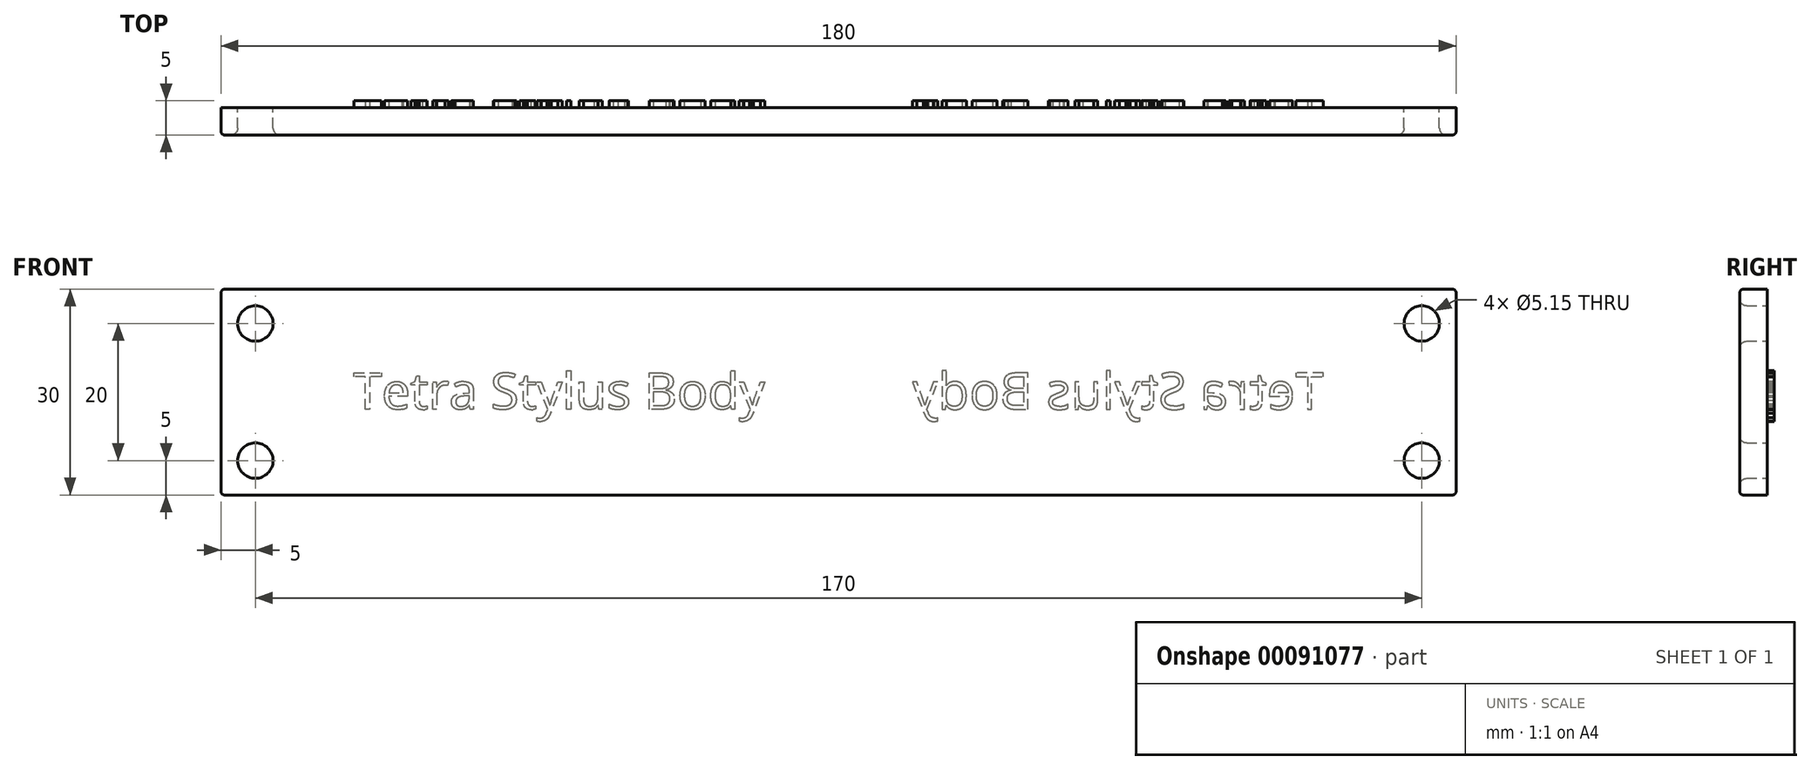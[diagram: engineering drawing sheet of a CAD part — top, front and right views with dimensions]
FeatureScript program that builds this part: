
annotation { "Feature Type Name" : "Feature", "Feature Type Description" : "" }
export const myFeature = defineFeature(function(context is Context, id is Id, definition is map)
    precondition{}
    {
        {
            var Q0;
            Q0=qCreatedBy(makeId("Front.planeOp"),FACE);
            var sketch = newSketch(context, id + "F0", { "sketchPlane" : qUnion([Q0])});
            skLineSegment(sketch, "E0.bottom", {"start": v(-90, -15) * mm, "end": v(90, -15) * mm});
            skLineSegment(sketch, "E0.top", {"start": v(-90, 15) * mm, "end": v(90, 15) * mm});
            skLineSegment(sketch, "E0.left", {"start": v(-90, -15) * mm, "end": v(-90, 15) * mm});
            skLineSegment(sketch, "E0.right", {"start": v(90, -15) * mm, "end": v(90, 15) * mm});
            skPoint(sketch, "E0.middle", {"position": v(0, 0) * mm});
            skCircle(sketch, "E1", {"center": v(-85, 10) * mm, "radius": 2.58 * mm});
            skPoint(sketch, "E2.start.orphan", {"position": v(-90, 0) * mm});
            skPoint(sketch, "E3.orphan", {"position": v(0, 15) * mm});
            skPoint(sketch, "E4.end.orphan", {"position": v(0, -15) * mm});
            skLineSegment(sketch, "E5", {"start": v(-90, 0) * mm, "end": v(0, 0) * mm, "construction": true});
            skLineSegment(sketch, "E6", {"start": v(0, 15) * mm, "end": v(0, -15) * mm, "construction": true});
            skCircle(sketch, "E7.MirrorC", {"center": v(-85, -10) * mm, "radius": 2.58 * mm});
            skCircle(sketch, "E8.MirrorC", {"center": v(85, 10) * mm, "radius": 2.58 * mm});
            skCircle(sketch, "E9.MirrorC", {"center": v(85, -10) * mm, "radius": 2.58 * mm});
            skSolve(sketch);
        }
        {
            var Q0;
            Q0=makeQuery(id+"F0.imprint","IMPRINT",FACE,{"disambiguationData":[TD([[makeQuery(id+"F0.imprint","IMPRINT",EDGE,{"derivedFrom":sQuery(id+"F0.wireOp",EDGE,"E0.bottom")}),1.0]])]});
            extrude(context, id + "F1", {"entities" : qUnion([Q0]), "depth" : 4 * mm});
        }
        {
            var Q0;
            Q0=makeQuery(id+"F1.opExtrude","CAP_EDGE",EDGE,{"disambiguationData":[OSD([sQuery(id+"F0.wireOp",EDGE,"E1")])],"isStart":false});
            var Q1;
            Q1=makeQuery(id+"F1.opExtrude","CAP_EDGE",EDGE,{"disambiguationData":[OSD([sQuery(id+"F0.wireOp",EDGE,"f5b72a5b-8583-449a-bdbf-9ac5a681e1fd0.MirrorC")])],"isStart":false});
            var Q2;
            Q2=makeQuery(id+"F1.opExtrude","CAP_EDGE",EDGE,{"disambiguationData":[OSD([sQuery(id+"F0.wireOp",EDGE,"2623e306-60f4-4522-aa65-1e3e8c2cf5b60.MirrorC")])],"isStart":false});
            var Q3;
            Q3=makeQuery(id+"F1.opExtrude","CAP_EDGE",EDGE,{"disambiguationData":[OSD([sQuery(id+"F0.wireOp",EDGE,"be81a34d-1d50-4ce7-a7a8-4484a1701fac0.MirrorC")])],"isStart":false});
            var Q4;
            Q4=makeQuery(id+"F1.opExtrude","CAP_EDGE",EDGE,{"disambiguationData":[OSD([sQuery(id+"F0.wireOp",EDGE,"E7.MirrorC")])],"isStart":false});
            var Q5;
            Q5=makeQuery(id+"F1.opExtrude","CAP_EDGE",EDGE,{"disambiguationData":[OSD([sQuery(id+"F0.wireOp",EDGE,"E8.MirrorC")])],"isStart":false});
            var Q6;
            Q6=makeQuery(id+"F1.opExtrude","CAP_EDGE",EDGE,{"disambiguationData":[OSD([sQuery(id+"F0.wireOp",EDGE,"E9.MirrorC")])],"isStart":false});
            fillet(context, id + "F2", {"entities" : qUnion([Q0, Q1, Q2, Q3, Q4, Q5, Q6]), "radius" : 1 * mm, "tangentPropagation" : true, "allowEdgeOverflow" : false});
        }
        {
            var Q0;
            Q0=makeQuery(id+"F1.opExtrude","CAP_EDGE",EDGE,{"disambiguationData":[OSD([sQuery(id+"F0.wireOp",EDGE,"E0.top")])],"isStart":false});
            var Q1;
            Q1=makeQuery(id+"F1.opExtrude","CAP_EDGE",EDGE,{"disambiguationData":[OSD([sQuery(id+"F0.wireOp",EDGE,"E0.left")])],"isStart":false});
            var Q2;
            Q2=makeQuery(id+"F1.opExtrude","CAP_EDGE",EDGE,{"disambiguationData":[OSD([sQuery(id+"F0.wireOp",EDGE,"E0.bottom")])],"isStart":false});
            var Q3;
            Q3=makeQuery(id+"F1.opExtrude","CAP_EDGE",EDGE,{"disambiguationData":[OSD([sQuery(id+"F0.wireOp",EDGE,"E0.right")])],"isStart":false});
            var Q4;
            Q4=makeQuery(id+"F1.opExtrude","SWEPT_EDGE",EDGE,{"disambiguationData":[OSD([sQuery(id+"F0.wireOp",EDGE,"E0.top"),sQuery(id+"F0.wireOp",EDGE,"E0.left")])]});
            var Q5;
            Q5=makeQuery(id+"F1.opExtrude","SWEPT_EDGE",EDGE,{"disambiguationData":[OSD([sQuery(id+"F0.wireOp",EDGE,"E0.bottom"),sQuery(id+"F0.wireOp",EDGE,"E0.left")])]});
            var Q6;
            Q6=makeQuery(id+"F1.opExtrude","SWEPT_EDGE",EDGE,{"disambiguationData":[OSD([sQuery(id+"F0.wireOp",EDGE,"E0.top"),sQuery(id+"F0.wireOp",EDGE,"E0.right")])]});
            var Q7;
            Q7=makeQuery(id+"F1.opExtrude","SWEPT_EDGE",EDGE,{"disambiguationData":[OSD([sQuery(id+"F0.wireOp",EDGE,"E0.bottom"),sQuery(id+"F0.wireOp",EDGE,"E0.right")])]});
            fillet(context, id + "F3", {"entities" : qUnion([Q0, Q1, Q2, Q3, Q4, Q5, Q6, Q7]), "radius" : .5 * mm, "tangentPropagation" : true, "allowEdgeOverflow" : false});
        }
        {
            var Q0;
            Q0=makeQuery(id+"F1.opExtrude","CAP_FACE",FACE,{"disambiguationData":[OSD([sQuery(id+"F0.wireOp",EDGE,"E0.bottom"),sQuery(id+"F0.wireOp",EDGE,"E0.top"),sQuery(id+"F0.wireOp",EDGE,"E0.left"),sQuery(id+"F0.wireOp",EDGE,"E0.right"),sQuery(id+"F0.wireOp",EDGE,"E1"),sQuery(id+"F0.wireOp",EDGE,"E7.MirrorC"),sQuery(id+"F0.wireOp",EDGE,"E8.MirrorC"),sQuery(id+"F0.wireOp",EDGE,"E9.MirrorC")])],"isStart":true});
            var sketch = newSketch(context, id + "F4", { "sketchPlane" : qUnion([Q0])});
            skText(sketch, "E10", { "text": "Tetra Stylus Body", "fontName": "OpenSans-Regular.ttf"});
            skLineSegment(sketch, "E11", {"start": v(0, 15) * mm, "end": v(0, -15) * mm, "construction": true});
            const initialGuessF4  = {"E10": [-0.0707, -0.0025, 1, 0, 0.00535]};
            skSetInitialGuess(sketch, initialGuessF4);
            skSolve(sketch);
        }
        {
            var Q0;
            Q0=qSketchRegion(id+"F4",true);
            extrude(context, id + "F5", {"entities" : qUnion([Q0]), "operationType" : NewBodyOperationType.ADD, "depth" : 1 * mm});
        }
        {
            var Q0;
            Q0=makeQuery(id+"F1.opExtrude","SWEPT_BODY",BODY,{"disambiguationData":[OSD([sQuery(id+"F0.wireOp",EDGE,"E0.bottom"),sQuery(id+"F0.wireOp",EDGE,"E0.top"),sQuery(id+"F0.wireOp",EDGE,"E0.left"),sQuery(id+"F0.wireOp",EDGE,"E0.right"),sQuery(id+"F0.wireOp",EDGE,"E1"),sQuery(id+"F0.wireOp",EDGE,"E7.MirrorC"),sQuery(id+"F0.wireOp",EDGE,"E8.MirrorC"),sQuery(id+"F0.wireOp",EDGE,"E9.MirrorC")])]});
            var Q1;
            Q1=makeQuery(id+"F5.opExtrude","SWEPT_FACE",FACE,{"disambiguationData":[OSD([sQuery(id+"F4.wireOp",EDGE,"E10.sketch_text.stroke-94")])]});
            var Q2;
            Q2=makeQuery(id+"F5.opExtrude","SWEPT_FACE",FACE,{"disambiguationData":[OSD([sQuery(id+"F4.wireOp",EDGE,"E10.sketch_text.stroke-169")])]});
            var Q3;
            Q3=makeQuery(id+"F5.opExtrude","SWEPT_FACE",FACE,{"disambiguationData":[OSD([sQuery(id+"F4.wireOp",EDGE,"E10.sketch_text.stroke-185")])]});
            var Q4;
            Q4=makeQuery(id+"F5.opExtrude","SWEPT_FACE",FACE,{"disambiguationData":[OSD([sQuery(id+"F4.wireOp",EDGE,"E10.sketch_text.stroke-125")])]});
            var Q5;
            Q5=makeQuery(id+"F5.opExtrude","SWEPT_FACE",FACE,{"disambiguationData":[OSD([sQuery(id+"F4.wireOp",EDGE,"E10.sketch_text.stroke-155")])]});
            var Q6;
            Q6=makeQuery(id+"F5.opExtrude","SWEPT_FACE",FACE,{"disambiguationData":[OSD([sQuery(id+"F4.wireOp",EDGE,"E10.sketch_text.stroke-65")])]});
            var Q7;
            Q7=makeQuery(id+"F5.opExtrude","SWEPT_FACE",FACE,{"disambiguationData":[OSD([sQuery(id+"F4.wireOp",EDGE,"E10.sketch_text.stroke-81")])]});
            var Q8;
            Q8=makeQuery(id+"F5.opExtrude","SWEPT_FACE",FACE,{"disambiguationData":[OSD([sQuery(id+"F4.wireOp",EDGE,"E10.sketch_text.stroke-67")])]});
            var Q9;
            Q9=makeQuery(id+"F5.opExtrude","SWEPT_FACE",FACE,{"disambiguationData":[OSD([sQuery(id+"F4.wireOp",EDGE,"E10.sketch_text.stroke-99")])]});
            var Q10;
            Q10=makeQuery(id+"F5.opExtrude","SWEPT_FACE",FACE,{"disambiguationData":[OSD([sQuery(id+"F4.wireOp",EDGE,"E10.sketch_text.stroke-127")])]});
            var Q11;
            Q11=makeQuery(id+"F5.opExtrude","SWEPT_FACE",FACE,{"disambiguationData":[OSD([sQuery(id+"F4.wireOp",EDGE,"E10.sketch_text.stroke-10")])]});
            var Q12;
            Q12=makeQuery(id+"F5.opExtrude","CAP_FACE",FACE,{"disambiguationData":[OSD([sQuery(id+"F4.wireOp",EDGE,"E10.sketch_text.stroke-9"),sQuery(id+"F4.wireOp",EDGE,"E10.sketch_text.stroke-10"),sQuery(id+"F4.wireOp",EDGE,"E10.sketch_text.stroke-11"),sQuery(id+"F4.wireOp",EDGE,"E10.sketch_text.stroke-12")])],"isStart":false});
            var Q13;
            Q13=makeQuery(id+"F5.opExtrude","SWEPT_FACE",FACE,{"disambiguationData":[OSD([sQuery(id+"F4.wireOp",EDGE,"E10.sketch_text.stroke-154")])]});
            var Q14;
            Q14=makeQuery(id+"F5.opExtrude","SWEPT_FACE",FACE,{"disambiguationData":[OSD([sQuery(id+"F4.wireOp",EDGE,"E10.sketch_text.stroke-1")])]});
            var Q15;
            Q15=makeQuery(id+"F5.opExtrude","CAP_FACE",FACE,{"disambiguationData":[OSD([sQuery(id+"F4.wireOp",EDGE,"E10.sketch_text.stroke-124"),sQuery(id+"F4.wireOp",EDGE,"E10.sketch_text.stroke-125"),sQuery(id+"F4.wireOp",EDGE,"E10.sketch_text.stroke-126"),sQuery(id+"F4.wireOp",EDGE,"E10.sketch_text.stroke-127"),sQuery(id+"F4.wireOp",EDGE,"E10.sketch_text.stroke-128"),sQuery(id+"F4.wireOp",EDGE,"E10.sketch_text.stroke-129"),sQuery(id+"F4.wireOp",EDGE,"E10.sketch_text.stroke-130"),sQuery(id+"F4.wireOp",EDGE,"E10.sketch_text.stroke-131"),sQuery(id+"F4.wireOp",EDGE,"E10.sketch_text.stroke-132"),sQuery(id+"F4.wireOp",EDGE,"E10.sketch_text.stroke-133"),sQuery(id+"F4.wireOp",EDGE,"E10.sketch_text.stroke-134"),sQuery(id+"F4.wireOp",EDGE,"E10.sketch_text.stroke-135"),sQuery(id+"F4.wireOp",EDGE,"E10.sketch_text.stroke-136"),sQuery(id+"F4.wireOp",EDGE,"E10.sketch_text.stroke-137"),sQuery(id+"F4.wireOp",EDGE,"E10.sketch_text.stroke-138")])],"isStart":false});
            var Q16;
            Q16=makeQuery(id+"F5.opExtrude","CAP_FACE",FACE,{"disambiguationData":[OSD([sQuery(id+"F4.wireOp",EDGE,"E10.sketch_text.stroke-34"),sQuery(id+"F4.wireOp",EDGE,"E10.sketch_text.stroke-35"),sQuery(id+"F4.wireOp",EDGE,"E10.sketch_text.stroke-36"),sQuery(id+"F4.wireOp",EDGE,"E10.sketch_text.stroke-37"),sQuery(id+"F4.wireOp",EDGE,"E10.sketch_text.stroke-38"),sQuery(id+"F4.wireOp",EDGE,"E10.sketch_text.stroke-39"),sQuery(id+"F4.wireOp",EDGE,"E10.sketch_text.stroke-40"),sQuery(id+"F4.wireOp",EDGE,"E10.sketch_text.stroke-41"),sQuery(id+"F4.wireOp",EDGE,"E10.sketch_text.stroke-42"),sQuery(id+"F4.wireOp",EDGE,"E10.sketch_text.stroke-43"),sQuery(id+"F4.wireOp",EDGE,"E10.sketch_text.stroke-44"),sQuery(id+"F4.wireOp",EDGE,"E10.sketch_text.stroke-45"),sQuery(id+"F4.wireOp",EDGE,"E10.sketch_text.stroke-46"),sQuery(id+"F4.wireOp",EDGE,"E10.sketch_text.stroke-47"),sQuery(id+"F4.wireOp",EDGE,"E10.sketch_text.stroke-48"),sQuery(id+"F4.wireOp",EDGE,"E10.sketch_text.stroke-49"),sQuery(id+"F4.wireOp",EDGE,"E10.sketch_text.stroke-50"),sQuery(id+"F4.wireOp",EDGE,"E10.sketch_text.stroke-51"),sQuery(id+"F4.wireOp",EDGE,"E10.sketch_text.stroke-52"),sQuery(id+"F4.wireOp",EDGE,"E10.sketch_text.stroke-53"),sQuery(id+"F4.wireOp",EDGE,"E10.sketch_text.stroke-54"),sQuery(id+"F4.wireOp",EDGE,"E10.sketch_text.stroke-55"),sQuery(id+"F4.wireOp",EDGE,"E10.sketch_text.stroke-56"),sQuery(id+"F4.wireOp",EDGE,"E10.sketch_text.stroke-57"),sQuery(id+"F4.wireOp",EDGE,"E10.sketch_text.stroke-58"),sQuery(id+"F4.wireOp",EDGE,"E10.sketch_text.stroke-59"),sQuery(id+"F4.wireOp",EDGE,"E10.sketch_text.stroke-60")])],"isStart":false});
            var Q17;
            Q17=makeQuery(id+"F5.opExtrude","SWEPT_FACE",FACE,{"disambiguationData":[OSD([sQuery(id+"F4.wireOp",EDGE,"E10.sketch_text.stroke-50")])]});
            var Q18;
            Q18=makeQuery(id+"F5.opExtrude","SWEPT_FACE",FACE,{"disambiguationData":[OSD([sQuery(id+"F4.wireOp",EDGE,"E10.sketch_text.stroke-2")])]});
            var Q19;
            Q19=makeQuery(id+"F5.opExtrude","SWEPT_FACE",FACE,{"disambiguationData":[OSD([sQuery(id+"F4.wireOp",EDGE,"E10.sketch_text.stroke-3")])]});
            var Q20;
            Q20=makeQuery(id+"F5.opExtrude","SWEPT_FACE",FACE,{"disambiguationData":[OSD([sQuery(id+"F4.wireOp",EDGE,"E10.sketch_text.stroke-5")])]});
            var Q21;
            Q21=makeQuery(id+"F5.opExtrude","SWEPT_FACE",FACE,{"disambiguationData":[OSD([sQuery(id+"F4.wireOp",EDGE,"E10.sketch_text.stroke-8")])]});
            var Q22;
            Q22=makeQuery(id+"F5.opExtrude","SWEPT_FACE",FACE,{"disambiguationData":[OSD([sQuery(id+"F4.wireOp",EDGE,"E10.sketch_text.stroke-98")])]});
            var Q23;
            Q23=makeQuery(id+"F5.opExtrude","SWEPT_FACE",FACE,{"disambiguationData":[OSD([sQuery(id+"F4.wireOp",EDGE,"E10.sketch_text.stroke-66")])]});
            var Q24;
            Q24=makeQuery(id+"F5.opExtrude","SWEPT_FACE",FACE,{"disambiguationData":[OSD([sQuery(id+"F4.wireOp",EDGE,"E10.sketch_text.stroke-153")])]});
            var Q25;
            Q25=makeQuery(id+"F5.opExtrude","SWEPT_FACE",FACE,{"disambiguationData":[OSD([sQuery(id+"F4.wireOp",EDGE,"E10.sketch_text.stroke-126")])]});
            var Q26;
            Q26=makeQuery(id+"F5.opExtrude","SWEPT_FACE",FACE,{"disambiguationData":[OSD([sQuery(id+"F4.wireOp",EDGE,"E10.sketch_text.stroke-183")])]});
            var Q27;
            Q27=makeQuery(id+"F5.opExtrude","SWEPT_FACE",FACE,{"disambiguationData":[OSD([sQuery(id+"F4.wireOp",EDGE,"E10.sketch_text.stroke-109")])]});
            var Q28;
            Q28=makeQuery(id+"F5.opExtrude","SWEPT_FACE",FACE,{"disambiguationData":[OSD([sQuery(id+"F4.wireOp",EDGE,"E10.sketch_text.stroke-186")])]});
            var Q29;
            Q29=makeQuery(id+"F5.opExtrude","SWEPT_FACE",FACE,{"disambiguationData":[OSD([sQuery(id+"F4.wireOp",EDGE,"E10.sketch_text.stroke-79")])]});
            var Q30;
            Q30=makeQuery(id+"F5.opExtrude","SWEPT_FACE",FACE,{"disambiguationData":[OSD([sQuery(id+"F4.wireOp",EDGE,"E10.sketch_text.stroke-110")])]});
            var Q31;
            Q31=makeQuery(id+"F5.opExtrude","SWEPT_FACE",FACE,{"disambiguationData":[OSD([sQuery(id+"F4.wireOp",EDGE,"E10.sketch_text.stroke-38")])]});
            var Q32;
            Q32=makeQuery(id+"F5.opExtrude","SWEPT_FACE",FACE,{"disambiguationData":[OSD([sQuery(id+"F4.wireOp",EDGE,"E10.sketch_text.stroke-24")])]});
            var Q33;
            Q33=makeQuery(id+"F5.opExtrude","SWEPT_FACE",FACE,{"disambiguationData":[OSD([sQuery(id+"F4.wireOp",EDGE,"E10.sketch_text.stroke-12")])]});
            var Q34;
            Q34=makeQuery(id+"F5.opExtrude","SWEPT_FACE",FACE,{"disambiguationData":[OSD([sQuery(id+"F4.wireOp",EDGE,"E10.sketch_text.stroke-100")])]});
            var Q35;
            Q35=makeQuery(id+"F5.opExtrude","SWEPT_FACE",FACE,{"disambiguationData":[OSD([sQuery(id+"F4.wireOp",EDGE,"E10.sketch_text.stroke-158")])]});
            var Q36;
            Q36=makeQuery(id+"F5.opExtrude","SWEPT_FACE",FACE,{"disambiguationData":[OSD([sQuery(id+"F4.wireOp",EDGE,"E10.sketch_text.stroke-142")])]});
            var Q37;
            Q37=makeQuery(id+"F5.opExtrude","SWEPT_FACE",FACE,{"disambiguationData":[OSD([sQuery(id+"F4.wireOp",EDGE,"E10.sketch_text.stroke-54")])]});
            var Q38;
            Q38=makeQuery(id+"F5.opExtrude","SWEPT_FACE",FACE,{"disambiguationData":[OSD([sQuery(id+"F4.wireOp",EDGE,"E10.sketch_text.stroke-25")])]});
            var Q39;
            Q39=makeQuery(id+"F5.opExtrude","SWEPT_FACE",FACE,{"disambiguationData":[OSD([sQuery(id+"F4.wireOp",EDGE,"E10.sketch_text.stroke-101")])]});
            var Q40;
            Q40=makeQuery(id+"F5.opExtrude","SWEPT_FACE",FACE,{"disambiguationData":[OSD([sQuery(id+"F4.wireOp",EDGE,"E10.sketch_text.stroke-69")])]});
            var Q41;
            Q41=makeQuery(id+"F5.opExtrude","SWEPT_FACE",FACE,{"disambiguationData":[OSD([sQuery(id+"F4.wireOp",EDGE,"E10.sketch_text.stroke-159")])]});
            var Q42;
            Q42=makeQuery(id+"F5.opExtrude","SWEPT_FACE",FACE,{"disambiguationData":[OSD([sQuery(id+"F4.wireOp",EDGE,"E10.sketch_text.stroke-85")])]});
            var Q43;
            Q43=makeQuery(id+"F5.opExtrude","SWEPT_FACE",FACE,{"disambiguationData":[OSD([sQuery(id+"F4.wireOp",EDGE,"E10.sketch_text.stroke-173")])]});
            var Q44;
            Q44=makeQuery(id+"F5.opExtrude","SWEPT_FACE",FACE,{"disambiguationData":[OSD([sQuery(id+"F4.wireOp",EDGE,"E10.sketch_text.stroke-40")])]});
            var Q45;
            Q45=makeQuery(id+"F5.opExtrude","SWEPT_FACE",FACE,{"disambiguationData":[OSD([sQuery(id+"F4.wireOp",EDGE,"E10.sketch_text.stroke-102")])]});
            var Q46;
            Q46=makeQuery(id+"F5.opExtrude","SWEPT_FACE",FACE,{"disambiguationData":[OSD([sQuery(id+"F4.wireOp",EDGE,"E10.sketch_text.stroke-86")])]});
            var Q47;
            Q47=makeQuery(id+"F5.opExtrude","SWEPT_FACE",FACE,{"disambiguationData":[OSD([sQuery(id+"F4.wireOp",EDGE,"E10.sketch_text.stroke-130")])]});
            var Q48;
            Q48=makeQuery(id+"F5.opExtrude","SWEPT_FACE",FACE,{"disambiguationData":[OSD([sQuery(id+"F4.wireOp",EDGE,"E10.sketch_text.stroke-103")])]});
            var Q49;
            Q49=makeQuery(id+"F5.opExtrude","SWEPT_FACE",FACE,{"disambiguationData":[OSD([sQuery(id+"F4.wireOp",EDGE,"E10.sketch_text.stroke-87")])]});
            var Q50;
            Q50=makeQuery(id+"F5.opExtrude","SWEPT_FACE",FACE,{"disambiguationData":[OSD([sQuery(id+"F4.wireOp",EDGE,"E10.sketch_text.stroke-145")])]});
            var Q51;
            Q51=makeQuery(id+"F5.opExtrude","SWEPT_FACE",FACE,{"disambiguationData":[OSD([sQuery(id+"F4.wireOp",EDGE,"E10.sketch_text.stroke-131")])]});
            var Q52;
            Q52=makeQuery(id+"F5.opExtrude","SWEPT_FACE",FACE,{"disambiguationData":[OSD([sQuery(id+"F4.wireOp",EDGE,"E10.sketch_text.stroke-28")])]});
            var Q53;
            Q53=makeQuery(id+"F5.opExtrude","SWEPT_FACE",FACE,{"disambiguationData":[OSD([sQuery(id+"F4.wireOp",EDGE,"E10.sketch_text.stroke-14")])]});
            var Q54;
            Q54=makeQuery(id+"F5.opExtrude","SWEPT_FACE",FACE,{"disambiguationData":[OSD([sQuery(id+"F4.wireOp",EDGE,"E10.sketch_text.stroke-88")])]});
            var Q55;
            Q55=makeQuery(id+"F5.opExtrude","SWEPT_FACE",FACE,{"disambiguationData":[OSD([sQuery(id+"F4.wireOp",EDGE,"E10.sketch_text.stroke-162")])]});
            var Q56;
            Q56=makeQuery(id+"F5.opExtrude","SWEPT_FACE",FACE,{"disambiguationData":[OSD([sQuery(id+"F4.wireOp",EDGE,"E10.sketch_text.stroke-176")])]});
            var Q57;
            Q57=makeQuery(id+"F5.opExtrude","SWEPT_FACE",FACE,{"disambiguationData":[OSD([sQuery(id+"F4.wireOp",EDGE,"E10.sketch_text.stroke-73")])]});
            var Q58;
            Q58=makeQuery(id+"F5.opExtrude","SWEPT_FACE",FACE,{"disambiguationData":[OSD([sQuery(id+"F4.wireOp",EDGE,"E10.sketch_text.stroke-59")])]});
            var Q59;
            Q59=makeQuery(id+"F5.opExtrude","SWEPT_FACE",FACE,{"disambiguationData":[OSD([sQuery(id+"F4.wireOp",EDGE,"E10.sketch_text.stroke-133")])]});
            var Q60;
            Q60=makeQuery(id+"F5.opExtrude","SWEPT_FACE",FACE,{"disambiguationData":[OSD([sQuery(id+"F4.wireOp",EDGE,"E10.sketch_text.stroke-119")])]});
            var Q61;
            Q61=makeQuery(id+"F5.opExtrude","SWEPT_FACE",FACE,{"disambiguationData":[OSD([sQuery(id+"F4.wireOp",EDGE,"E10.sketch_text.stroke-74")])]});
            var Q62;
            Q62=makeQuery(id+"F5.opExtrude","SWEPT_FACE",FACE,{"disambiguationData":[OSD([sQuery(id+"F4.wireOp",EDGE,"E10.sketch_text.stroke-44")])]});
            var Q63;
            Q63=makeQuery(id+"F5.opExtrude","SWEPT_FACE",FACE,{"disambiguationData":[OSD([sQuery(id+"F4.wireOp",EDGE,"E10.sketch_text.stroke-120")])]});
            var Q64;
            Q64=makeQuery(id+"F5.opExtrude","SWEPT_FACE",FACE,{"disambiguationData":[OSD([sQuery(id+"F4.wireOp",EDGE,"E10.sketch_text.stroke-90")])]});
            var Q65;
            Q65=makeQuery(id+"F5.opExtrude","SWEPT_FACE",FACE,{"disambiguationData":[OSD([sQuery(id+"F4.wireOp",EDGE,"E10.sketch_text.stroke-178")])]});
            var Q66;
            Q66=makeQuery(id+"F5.opExtrude","SWEPT_FACE",FACE,{"disambiguationData":[OSD([sQuery(id+"F4.wireOp",EDGE,"E10.sketch_text.stroke-45")])]});
            var Q67;
            Q67=makeQuery(id+"F5.opExtrude","SWEPT_FACE",FACE,{"disambiguationData":[OSD([sQuery(id+"F4.wireOp",EDGE,"E10.sketch_text.stroke-31")])]});
            var Q68;
            Q68=makeQuery(id+"F5.opExtrude","SWEPT_FACE",FACE,{"disambiguationData":[OSD([sQuery(id+"F4.wireOp",EDGE,"E10.sketch_text.stroke-135")])]});
            var Q69;
            Q69=makeQuery(id+"F5.opExtrude","SWEPT_FACE",FACE,{"disambiguationData":[OSD([sQuery(id+"F4.wireOp",EDGE,"E10.sketch_text.stroke-179")])]});
            var Q70;
            Q70=makeQuery(id+"F5.opExtrude","SWEPT_FACE",FACE,{"disambiguationData":[OSD([sQuery(id+"F4.wireOp",EDGE,"E10.sketch_text.stroke-165")])]});
            var Q71;
            Q71=makeQuery(id+"F5.opExtrude","SWEPT_FACE",FACE,{"disambiguationData":[OSD([sQuery(id+"F4.wireOp",EDGE,"E10.sketch_text.stroke-149")])]});
            var Q72;
            Q72=makeQuery(id+"F5.opExtrude","SWEPT_FACE",FACE,{"disambiguationData":[OSD([sQuery(id+"F4.wireOp",EDGE,"E10.sketch_text.stroke-136")])]});
            var Q73;
            Q73=makeQuery(id+"F5.opExtrude","SWEPT_FACE",FACE,{"disambiguationData":[OSD([sQuery(id+"F4.wireOp",EDGE,"E10.sketch_text.stroke-122")])]});
            var Q74;
            Q74=makeQuery(id+"F5.opExtrude","SWEPT_FACE",FACE,{"disambiguationData":[OSD([sQuery(id+"F4.wireOp",EDGE,"E10.sketch_text.stroke-106")])]});
            var Q75;
            Q75=makeQuery(id+"F5.opExtrude","SWEPT_FACE",FACE,{"disambiguationData":[OSD([sQuery(id+"F4.wireOp",EDGE,"E10.sketch_text.stroke-180")])]});
            var Q76;
            Q76=makeQuery(id+"F5.opExtrude","SWEPT_FACE",FACE,{"disambiguationData":[OSD([sQuery(id+"F4.wireOp",EDGE,"E10.sketch_text.stroke-166")])]});
            var Q77;
            Q77=makeQuery(id+"F5.opExtrude","SWEPT_FACE",FACE,{"disambiguationData":[OSD([sQuery(id+"F4.wireOp",EDGE,"E10.sketch_text.stroke-150")])]});
            var Q78;
            Q78=makeQuery(id+"F5.opExtrude","SWEPT_FACE",FACE,{"disambiguationData":[OSD([sQuery(id+"F4.wireOp",EDGE,"E10.sketch_text.stroke-76")])]});
            var Q79;
            Q79=makeQuery(id+"F5.opExtrude","SWEPT_FACE",FACE,{"disambiguationData":[OSD([sQuery(id+"F4.wireOp",EDGE,"E10.sketch_text.stroke-32")])]});
            var Q80;
            Q80=makeQuery(id+"F5.opExtrude","SWEPT_FACE",FACE,{"disambiguationData":[OSD([sQuery(id+"F4.wireOp",EDGE,"E10.sketch_text.stroke-181")])]});
            var Q81;
            Q81=makeQuery(id+"F5.opExtrude","SWEPT_FACE",FACE,{"disambiguationData":[OSD([sQuery(id+"F4.wireOp",EDGE,"E10.sketch_text.stroke-47")])]});
            var Q82;
            Q82=makeQuery(id+"F5.opExtrude","SWEPT_FACE",FACE,{"disambiguationData":[OSD([sQuery(id+"F4.wireOp",EDGE,"E10.sketch_text.stroke-123")])]});
            var Q83;
            Q83=makeQuery(id+"F5.opExtrude","SWEPT_FACE",FACE,{"disambiguationData":[OSD([sQuery(id+"F4.wireOp",EDGE,"E10.sketch_text.stroke-107")])]});
            var Q84;
            Q84=makeQuery(id+"F5.opExtrude","SWEPT_FACE",FACE,{"disambiguationData":[OSD([sQuery(id+"F4.wireOp",EDGE,"E10.sketch_text.stroke-48")])]});
            var Q85;
            Q85=makeQuery(id+"F5.opExtrude","SWEPT_FACE",FACE,{"disambiguationData":[OSD([sQuery(id+"F4.wireOp",EDGE,"E10.sketch_text.stroke-124")])]});
            var Q86;
            Q86=makeQuery(id+"F5.opExtrude","SWEPT_FACE",FACE,{"disambiguationData":[OSD([sQuery(id+"F4.wireOp",EDGE,"E10.sketch_text.stroke-108")])]});
            var Q87;
            Q87=makeQuery(id+"F5.opExtrude","CAP_FACE",FACE,{"disambiguationData":[OSD([sQuery(id+"F4.wireOp",EDGE,"E10.sketch_text.stroke-139"),sQuery(id+"F4.wireOp",EDGE,"E10.sketch_text.stroke-140"),sQuery(id+"F4.wireOp",EDGE,"E10.sketch_text.stroke-141"),sQuery(id+"F4.wireOp",EDGE,"E10.sketch_text.stroke-142"),sQuery(id+"F4.wireOp",EDGE,"E10.sketch_text.stroke-143"),sQuery(id+"F4.wireOp",EDGE,"E10.sketch_text.stroke-144"),sQuery(id+"F4.wireOp",EDGE,"E10.sketch_text.stroke-145"),sQuery(id+"F4.wireOp",EDGE,"E10.sketch_text.stroke-146"),sQuery(id+"F4.wireOp",EDGE,"E10.sketch_text.stroke-147"),sQuery(id+"F4.wireOp",EDGE,"E10.sketch_text.stroke-148"),sQuery(id+"F4.wireOp",EDGE,"E10.sketch_text.stroke-149"),sQuery(id+"F4.wireOp",EDGE,"E10.sketch_text.stroke-150"),sQuery(id+"F4.wireOp",EDGE,"E10.sketch_text.stroke-151"),sQuery(id+"F4.wireOp",EDGE,"E10.sketch_text.stroke-152"),sQuery(id+"F4.wireOp",EDGE,"E10.sketch_text.stroke-153"),sQuery(id+"F4.wireOp",EDGE,"E10.sketch_text.stroke-154"),sQuery(id+"F4.wireOp",EDGE,"E10.sketch_text.stroke-155"),sQuery(id+"F4.wireOp",EDGE,"E10.sketch_text.stroke-156"),sQuery(id+"F4.wireOp",EDGE,"E10.sketch_text.stroke-157"),sQuery(id+"F4.wireOp",EDGE,"E10.sketch_text.stroke-158"),sQuery(id+"F4.wireOp",EDGE,"E10.sketch_text.stroke-159"),sQuery(id+"F4.wireOp",EDGE,"E10.sketch_text.stroke-160"),sQuery(id+"F4.wireOp",EDGE,"E10.sketch_text.stroke-161"),sQuery(id+"F4.wireOp",EDGE,"E10.sketch_text.stroke-162"),sQuery(id+"F4.wireOp",EDGE,"E10.sketch_text.stroke-163"),sQuery(id+"F4.wireOp",EDGE,"E10.sketch_text.stroke-164"),sQuery(id+"F4.wireOp",EDGE,"E10.sketch_text.stroke-165")])],"isStart":false});
            var Q88;
            Q88=makeQuery(id+"F5.opExtrude","CAP_FACE",FACE,{"disambiguationData":[OSD([sQuery(id+"F4.wireOp",EDGE,"E10.sketch_text.stroke-21"),sQuery(id+"F4.wireOp",EDGE,"E10.sketch_text.stroke-22"),sQuery(id+"F4.wireOp",EDGE,"E10.sketch_text.stroke-23"),sQuery(id+"F4.wireOp",EDGE,"E10.sketch_text.stroke-24"),sQuery(id+"F4.wireOp",EDGE,"E10.sketch_text.stroke-25"),sQuery(id+"F4.wireOp",EDGE,"E10.sketch_text.stroke-26"),sQuery(id+"F4.wireOp",EDGE,"E10.sketch_text.stroke-27"),sQuery(id+"F4.wireOp",EDGE,"E10.sketch_text.stroke-28"),sQuery(id+"F4.wireOp",EDGE,"E10.sketch_text.stroke-29"),sQuery(id+"F4.wireOp",EDGE,"E10.sketch_text.stroke-30"),sQuery(id+"F4.wireOp",EDGE,"E10.sketch_text.stroke-31"),sQuery(id+"F4.wireOp",EDGE,"E10.sketch_text.stroke-32"),sQuery(id+"F4.wireOp",EDGE,"E10.sketch_text.stroke-33")])],"isStart":false});
            var Q89;
            Q89=makeQuery(id+"F5.opExtrude","SWEPT_FACE",FACE,{"disambiguationData":[OSD([sQuery(id+"F4.wireOp",EDGE,"E10.sketch_text.stroke-113")])]});
            var Q90;
            Q90=makeQuery(id+"F5.opExtrude","SWEPT_FACE",FACE,{"disambiguationData":[OSD([sQuery(id+"F4.wireOp",EDGE,"E10.sketch_text.stroke-37")])]});
            var Q91;
            Q91=makeQuery(id+"F5.opExtrude","SWEPT_FACE",FACE,{"disambiguationData":[OSD([sQuery(id+"F4.wireOp",EDGE,"E10.sketch_text.stroke-187")])]});
            var Q92;
            Q92=makeQuery(id+"F5.opExtrude","SWEPT_FACE",FACE,{"disambiguationData":[OSD([sQuery(id+"F4.wireOp",EDGE,"E10.sketch_text.stroke-0")])]});
            var Q93;
            Q93=makeQuery(id+"F5.opExtrude","SWEPT_FACE",FACE,{"disambiguationData":[OSD([sQuery(id+"F4.wireOp",EDGE,"E10.sketch_text.stroke-4")])]});
            var Q94;
            Q94=makeQuery(id+"F5.opExtrude","SWEPT_FACE",FACE,{"disambiguationData":[OSD([sQuery(id+"F4.wireOp",EDGE,"E10.sketch_text.stroke-82")])]});
            var Q95;
            Q95=makeQuery(id+"F5.opExtrude","SWEPT_FACE",FACE,{"disambiguationData":[OSD([sQuery(id+"F4.wireOp",EDGE,"E10.sketch_text.stroke-52")])]});
            var Q96;
            Q96=makeQuery(id+"F5.opExtrude","SWEPT_FACE",FACE,{"disambiguationData":[OSD([sQuery(id+"F4.wireOp",EDGE,"E10.sketch_text.stroke-49")])]});
            var Q97;
            Q97=makeQuery(id+"F5.opExtrude","SWEPT_FACE",FACE,{"disambiguationData":[OSD([sQuery(id+"F4.wireOp",EDGE,"E10.sketch_text.stroke-63")])]});
            var Q98;
            Q98=makeQuery(id+"F5.opExtrude","SWEPT_FACE",FACE,{"disambiguationData":[OSD([sQuery(id+"F4.wireOp",EDGE,"E10.sketch_text.stroke-21")])]});
            var Q99;
            Q99=makeQuery(id+"F5.opExtrude","SWEPT_FACE",FACE,{"disambiguationData":[OSD([sQuery(id+"F4.wireOp",EDGE,"E10.sketch_text.stroke-128")])]});
            var Q100;
            Q100=makeQuery(id+"F5.opExtrude","SWEPT_FACE",FACE,{"disambiguationData":[OSD([sQuery(id+"F4.wireOp",EDGE,"E10.sketch_text.stroke-55")])]});
            var Q101;
            Q101=makeQuery(id+"F5.opExtrude","SWEPT_FACE",FACE,{"disambiguationData":[OSD([sQuery(id+"F4.wireOp",EDGE,"E10.sketch_text.stroke-26")])]});
            var Q102;
            Q102=makeQuery(id+"F5.opExtrude","SWEPT_FACE",FACE,{"disambiguationData":[OSD([sQuery(id+"F4.wireOp",EDGE,"E10.sketch_text.stroke-174")])]});
            var Q103;
            Q103=makeQuery(id+"F5.opExtrude","SWEPT_FACE",FACE,{"disambiguationData":[OSD([sQuery(id+"F4.wireOp",EDGE,"E10.sketch_text.stroke-104")])]});
            var Q104;
            Q104=makeQuery(id+"F5.opExtrude","SWEPT_FACE",FACE,{"disambiguationData":[OSD([sQuery(id+"F4.wireOp",EDGE,"E10.sketch_text.stroke-72")])]});
            var Q105;
            Q105=makeQuery(id+"F5.opExtrude","SWEPT_FACE",FACE,{"disambiguationData":[OSD([sQuery(id+"F4.wireOp",EDGE,"E10.sketch_text.stroke-132")])]});
            var Q106;
            Q106=makeQuery(id+"F5.opExtrude","SWEPT_FACE",FACE,{"disambiguationData":[OSD([sQuery(id+"F4.wireOp",EDGE,"E10.sketch_text.stroke-43")])]});
            var Q107;
            Q107=makeQuery(id+"F5.opExtrude","SWEPT_FACE",FACE,{"disambiguationData":[OSD([sQuery(id+"F4.wireOp",EDGE,"E10.sketch_text.stroke-15")])]});
            var Q108;
            Q108=makeQuery(id+"F5.opExtrude","SWEPT_FACE",FACE,{"disambiguationData":[OSD([sQuery(id+"F4.wireOp",EDGE,"E10.sketch_text.stroke-89")])]});
            var Q109;
            Q109=makeQuery(id+"F5.opExtrude","SWEPT_FACE",FACE,{"disambiguationData":[OSD([sQuery(id+"F4.wireOp",EDGE,"E10.sketch_text.stroke-163")])]});
            var Q110;
            Q110=makeQuery(id+"F5.opExtrude","SWEPT_FACE",FACE,{"disambiguationData":[OSD([sQuery(id+"F4.wireOp",EDGE,"E10.sketch_text.stroke-30")])]});
            var Q111;
            Q111=makeQuery(id+"F5.opExtrude","SWEPT_FACE",FACE,{"disambiguationData":[OSD([sQuery(id+"F4.wireOp",EDGE,"E10.sketch_text.stroke-134")])]});
            var Q112;
            Q112=makeQuery(id+"F5.opExtrude","SWEPT_FACE",FACE,{"disambiguationData":[OSD([sQuery(id+"F4.wireOp",EDGE,"E10.sketch_text.stroke-121")])]});
            var Q113;
            Q113=makeQuery(id+"F5.opExtrude","CAP_FACE",FACE,{"disambiguationData":[OSD([sQuery(id+"F4.wireOp",EDGE,"E10.sketch_text.stroke-105"),sQuery(id+"F4.wireOp",EDGE,"E10.sketch_text.stroke-106"),sQuery(id+"F4.wireOp",EDGE,"E10.sketch_text.stroke-107"),sQuery(id+"F4.wireOp",EDGE,"E10.sketch_text.stroke-108"),sQuery(id+"F4.wireOp",EDGE,"E10.sketch_text.stroke-109"),sQuery(id+"F4.wireOp",EDGE,"E10.sketch_text.stroke-110"),sQuery(id+"F4.wireOp",EDGE,"E10.sketch_text.stroke-111"),sQuery(id+"F4.wireOp",EDGE,"E10.sketch_text.stroke-112"),sQuery(id+"F4.wireOp",EDGE,"E10.sketch_text.stroke-113"),sQuery(id+"F4.wireOp",EDGE,"E10.sketch_text.stroke-114"),sQuery(id+"F4.wireOp",EDGE,"E10.sketch_text.stroke-115"),sQuery(id+"F4.wireOp",EDGE,"E10.sketch_text.stroke-116"),sQuery(id+"F4.wireOp",EDGE,"E10.sketch_text.stroke-117"),sQuery(id+"F4.wireOp",EDGE,"E10.sketch_text.stroke-118"),sQuery(id+"F4.wireOp",EDGE,"E10.sketch_text.stroke-119"),sQuery(id+"F4.wireOp",EDGE,"E10.sketch_text.stroke-120"),sQuery(id+"F4.wireOp",EDGE,"E10.sketch_text.stroke-121"),sQuery(id+"F4.wireOp",EDGE,"E10.sketch_text.stroke-122"),sQuery(id+"F4.wireOp",EDGE,"E10.sketch_text.stroke-123")])],"isStart":false});
            var Q114;
            Q114=makeQuery(id+"F5.opExtrude","SWEPT_FACE",FACE,{"disambiguationData":[OSD([sQuery(id+"F4.wireOp",EDGE,"E10.sketch_text.stroke-92")])]});
            var Q115;
            Q115=makeQuery(id+"F5.opExtrude","SWEPT_FACE",FACE,{"disambiguationData":[OSD([sQuery(id+"F4.wireOp",EDGE,"E10.sketch_text.stroke-46")])]});
            var Q116;
            Q116=makeQuery(id+"F5.opExtrude","CAP_FACE",FACE,{"disambiguationData":[OSD([sQuery(id+"F4.wireOp",EDGE,"E10.sketch_text.stroke-61"),sQuery(id+"F4.wireOp",EDGE,"E10.sketch_text.stroke-62"),sQuery(id+"F4.wireOp",EDGE,"E10.sketch_text.stroke-63"),sQuery(id+"F4.wireOp",EDGE,"E10.sketch_text.stroke-64"),sQuery(id+"F4.wireOp",EDGE,"E10.sketch_text.stroke-65"),sQuery(id+"F4.wireOp",EDGE,"E10.sketch_text.stroke-66"),sQuery(id+"F4.wireOp",EDGE,"E10.sketch_text.stroke-67"),sQuery(id+"F4.wireOp",EDGE,"E10.sketch_text.stroke-68"),sQuery(id+"F4.wireOp",EDGE,"E10.sketch_text.stroke-69"),sQuery(id+"F4.wireOp",EDGE,"E10.sketch_text.stroke-70"),sQuery(id+"F4.wireOp",EDGE,"E10.sketch_text.stroke-71"),sQuery(id+"F4.wireOp",EDGE,"E10.sketch_text.stroke-72"),sQuery(id+"F4.wireOp",EDGE,"E10.sketch_text.stroke-73"),sQuery(id+"F4.wireOp",EDGE,"E10.sketch_text.stroke-74"),sQuery(id+"F4.wireOp",EDGE,"E10.sketch_text.stroke-75"),sQuery(id+"F4.wireOp",EDGE,"E10.sketch_text.stroke-76"),sQuery(id+"F4.wireOp",EDGE,"E10.sketch_text.stroke-77"),sQuery(id+"F4.wireOp",EDGE,"E10.sketch_text.stroke-78"),sQuery(id+"F4.wireOp",EDGE,"E10.sketch_text.stroke-79"),sQuery(id+"F4.wireOp",EDGE,"E10.sketch_text.stroke-80"),sQuery(id+"F4.wireOp",EDGE,"E10.sketch_text.stroke-81"),sQuery(id+"F4.wireOp",EDGE,"E10.sketch_text.stroke-82"),sQuery(id+"F4.wireOp",EDGE,"E10.sketch_text.stroke-83"),sQuery(id+"F4.wireOp",EDGE,"E10.sketch_text.stroke-84"),sQuery(id+"F4.wireOp",EDGE,"E10.sketch_text.stroke-85"),sQuery(id+"F4.wireOp",EDGE,"E10.sketch_text.stroke-86"),sQuery(id+"F4.wireOp",EDGE,"E10.sketch_text.stroke-87"),sQuery(id+"F4.wireOp",EDGE,"E10.sketch_text.stroke-88"),sQuery(id+"F4.wireOp",EDGE,"E10.sketch_text.stroke-89"),sQuery(id+"F4.wireOp",EDGE,"E10.sketch_text.stroke-90"),sQuery(id+"F4.wireOp",EDGE,"E10.sketch_text.stroke-91"),sQuery(id+"F4.wireOp",EDGE,"E10.sketch_text.stroke-92"),sQuery(id+"F4.wireOp",EDGE,"E10.sketch_text.stroke-93"),sQuery(id+"F4.wireOp",EDGE,"E10.sketch_text.stroke-94"),sQuery(id+"F4.wireOp",EDGE,"E10.sketch_text.stroke-95"),sQuery(id+"F4.wireOp",EDGE,"E10.sketch_text.stroke-96"),sQuery(id+"F4.wireOp",EDGE,"E10.sketch_text.stroke-97"),sQuery(id+"F4.wireOp",EDGE,"E10.sketch_text.stroke-98"),sQuery(id+"F4.wireOp",EDGE,"E10.sketch_text.stroke-99"),sQuery(id+"F4.wireOp",EDGE,"E10.sketch_text.stroke-100"),sQuery(id+"F4.wireOp",EDGE,"E10.sketch_text.stroke-101"),sQuery(id+"F4.wireOp",EDGE,"E10.sketch_text.stroke-102"),sQuery(id+"F4.wireOp",EDGE,"E10.sketch_text.stroke-103"),sQuery(id+"F4.wireOp",EDGE,"E10.sketch_text.stroke-104")])],"isStart":false});
            var Q117;
            Q117=makeQuery(id+"F5.opExtrude","SWEPT_FACE",FACE,{"disambiguationData":[OSD([sQuery(id+"F4.wireOp",EDGE,"E10.sketch_text.stroke-33")])]});
            var Q118;
            Q118=makeQuery(id+"F5.opExtrude","SWEPT_FACE",FACE,{"disambiguationData":[OSD([sQuery(id+"F4.wireOp",EDGE,"E10.sketch_text.stroke-93")])]});
            var Q119;
            Q119=makeQuery(id+"F5.opExtrude","SWEPT_FACE",FACE,{"disambiguationData":[OSD([sQuery(id+"F4.wireOp",EDGE,"E10.sketch_text.stroke-34")])]});
            var Q120;
            Q120=makeQuery(id+"F5.opExtrude","SWEPT_FACE",FACE,{"disambiguationData":[OSD([sQuery(id+"F4.wireOp",EDGE,"E10.sketch_text.stroke-152")])]});
            var Q121;
            Q121=makeQuery(id+"F5.opExtrude","SWEPT_FACE",FACE,{"disambiguationData":[OSD([sQuery(id+"F4.wireOp",EDGE,"E10.sketch_text.stroke-51")])]});
            var Q122;
            Q122=makeQuery(id+"F5.opExtrude","SWEPT_FACE",FACE,{"disambiguationData":[OSD([sQuery(id+"F4.wireOp",EDGE,"E10.sketch_text.stroke-6")])]});
            var Q123;
            Q123=makeQuery(id+"F5.opExtrude","SWEPT_FACE",FACE,{"disambiguationData":[OSD([sQuery(id+"F4.wireOp",EDGE,"E10.sketch_text.stroke-7")])]});
            var Q124;
            Q124=makeQuery(id+"F5.opExtrude","SWEPT_FACE",FACE,{"disambiguationData":[OSD([sQuery(id+"F4.wireOp",EDGE,"E10.sketch_text.stroke-156")])]});
            var Q125;
            Q125=makeQuery(id+"F5.opExtrude","SWEPT_FACE",FACE,{"disambiguationData":[OSD([sQuery(id+"F4.wireOp",EDGE,"E10.sketch_text.stroke-112")])]});
            var Q126;
            Q126=makeQuery(id+"F5.boolean.opBoolean","SPLIT",FACE,{"disambiguationData":[TD([makeQuery(id+"F5.opExtrude","SWEPT_FACE",FACE,{"disambiguationData":[OSD([sQuery(id+"F4.wireOp",EDGE,"E10.sketch_text.stroke-182")])]})])],"derivedFrom":makeQuery(id+"F1.opExtrude","CAP_FACE",FACE,{"disambiguationData":[OSD([sQuery(id+"F0.wireOp",EDGE,"E0.bottom"),sQuery(id+"F0.wireOp",EDGE,"E0.top"),sQuery(id+"F0.wireOp",EDGE,"E0.left"),sQuery(id+"F0.wireOp",EDGE,"E0.right"),sQuery(id+"F0.wireOp",EDGE,"E1"),sQuery(id+"F0.wireOp",EDGE,"E7.MirrorC"),sQuery(id+"F0.wireOp",EDGE,"E8.MirrorC"),sQuery(id+"F0.wireOp",EDGE,"E9.MirrorC")])],"isStart":true})});
            var Q127;
            Q127=makeQuery(id+"F5.opExtrude","SWEPT_FACE",FACE,{"disambiguationData":[OSD([sQuery(id+"F4.wireOp",EDGE,"E10.sketch_text.stroke-96")])]});
            var Q128;
            Q128=makeQuery(id+"F5.opExtrude","SWEPT_FACE",FACE,{"disambiguationData":[OSD([sQuery(id+"F4.wireOp",EDGE,"E10.sketch_text.stroke-114")])]});
            var Q129;
            Q129=makeQuery(id+"F5.opExtrude","SWEPT_FACE",FACE,{"disambiguationData":[OSD([sQuery(id+"F4.wireOp",EDGE,"E10.sketch_text.stroke-39")])]});
            var Q130;
            Q130=makeQuery(id+"F5.opExtrude","SWEPT_FACE",FACE,{"disambiguationData":[OSD([sQuery(id+"F4.wireOp",EDGE,"E10.sketch_text.stroke-13")])]});
            var Q131;
            Q131=makeQuery(id+"F5.opExtrude","SWEPT_FACE",FACE,{"disambiguationData":[OSD([sQuery(id+"F4.wireOp",EDGE,"E10.sketch_text.stroke-115")])]});
            var Q132;
            Q132=makeQuery(id+"F5.opExtrude","SWEPT_FACE",FACE,{"disambiguationData":[OSD([sQuery(id+"F4.wireOp",EDGE,"E10.sketch_text.stroke-56")])]});
            var Q133;
            Q133=makeQuery(id+"F5.opExtrude","SWEPT_FACE",FACE,{"disambiguationData":[OSD([sQuery(id+"F4.wireOp",EDGE,"E10.sketch_text.stroke-144")])]});
            var Q134;
            Q134=makeQuery(id+"F5.opExtrude","SWEPT_FACE",FACE,{"disambiguationData":[OSD([sQuery(id+"F4.wireOp",EDGE,"E10.sketch_text.stroke-190")])]});
            var Q135;
            Q135=makeQuery(id+"F5.opExtrude","SWEPT_FACE",FACE,{"disambiguationData":[OSD([sQuery(id+"F4.wireOp",EDGE,"E10.sketch_text.stroke-116")])]});
            var Q136;
            Q136=makeQuery(id+"F5.opExtrude","SWEPT_FACE",FACE,{"disambiguationData":[OSD([sQuery(id+"F4.wireOp",EDGE,"E10.sketch_text.stroke-41")])]});
            var Q137;
            Q137=makeQuery(id+"F5.opExtrude","SWEPT_FACE",FACE,{"disambiguationData":[OSD([sQuery(id+"F4.wireOp",EDGE,"E10.sketch_text.stroke-161")])]});
            var Q138;
            Q138=makeQuery(id+"F5.opExtrude","SWEPT_FACE",FACE,{"disambiguationData":[OSD([sQuery(id+"F4.wireOp",EDGE,"E10.sketch_text.stroke-146")])]});
            var Q139;
            Q139=makeQuery(id+"F5.opExtrude","SWEPT_FACE",FACE,{"disambiguationData":[OSD([sQuery(id+"F4.wireOp",EDGE,"E10.sketch_text.stroke-58")])]});
            var Q140;
            Q140=makeQuery(id+"F5.opExtrude","SWEPT_FACE",FACE,{"disambiguationData":[OSD([sQuery(id+"F4.wireOp",EDGE,"E10.sketch_text.stroke-105")])]});
            var Q141;
            Q141=makeQuery(id+"F5.opExtrude","SWEPT_FACE",FACE,{"disambiguationData":[OSD([sQuery(id+"F4.wireOp",EDGE,"E10.sketch_text.stroke-177")])]});
            var Q142;
            Q142=makeQuery(id+"F5.opExtrude","SWEPT_FACE",FACE,{"disambiguationData":[OSD([sQuery(id+"F4.wireOp",EDGE,"E10.sketch_text.stroke-77")])]});
            var Q143;
            Q143=makeQuery(id+"F5.opExtrude","SWEPT_FACE",FACE,{"disambiguationData":[OSD([sQuery(id+"F4.wireOp",EDGE,"E10.sketch_text.stroke-138")])]});
            var Q144;
            Q144=makeQuery(id+"F5.opExtrude","SWEPT_FACE",FACE,{"disambiguationData":[OSD([sQuery(id+"F4.wireOp",EDGE,"E10.sketch_text.stroke-111")])]});
            var Q145;
            Q145=makeQuery(id+"F5.opExtrude","SWEPT_FACE",FACE,{"disambiguationData":[OSD([sQuery(id+"F4.wireOp",EDGE,"E10.sketch_text.stroke-53")])]});
            var Q146;
            Q146=makeQuery(id+"F5.opExtrude","SWEPT_FACE",FACE,{"disambiguationData":[OSD([sQuery(id+"F4.wireOp",EDGE,"E10.sketch_text.stroke-141")])]});
            var Q147;
            Q147=makeQuery(id+"F5.opExtrude","SWEPT_FACE",FACE,{"disambiguationData":[OSD([sQuery(id+"F4.wireOp",EDGE,"E10.sketch_text.stroke-157")])]});
            var Q148;
            Q148=makeQuery(id+"F5.opExtrude","SWEPT_FACE",FACE,{"disambiguationData":[OSD([sQuery(id+"F4.wireOp",EDGE,"E10.sketch_text.stroke-64")])]});
            var Q149;
            Q149=makeQuery(id+"F5.boolean.opBoolean","SPLIT",FACE,{"disambiguationData":[TD([makeQuery(id+"F5.opExtrude","SWEPT_FACE",FACE,{"disambiguationData":[OSD([sQuery(id+"F4.wireOp",EDGE,"E10.sketch_text.stroke-53")])]})])],"derivedFrom":makeQuery(id+"F1.opExtrude","CAP_FACE",FACE,{"disambiguationData":[OSD([sQuery(id+"F0.wireOp",EDGE,"E0.bottom"),sQuery(id+"F0.wireOp",EDGE,"E0.top"),sQuery(id+"F0.wireOp",EDGE,"E0.left"),sQuery(id+"F0.wireOp",EDGE,"E0.right"),sQuery(id+"F0.wireOp",EDGE,"E1"),sQuery(id+"F0.wireOp",EDGE,"E7.MirrorC"),sQuery(id+"F0.wireOp",EDGE,"E8.MirrorC"),sQuery(id+"F0.wireOp",EDGE,"E9.MirrorC")])],"isStart":true})});
            var Q150;
            Q150=makeQuery(id+"F5.opExtrude","SWEPT_FACE",FACE,{"disambiguationData":[OSD([sQuery(id+"F4.wireOp",EDGE,"E10.sketch_text.stroke-36")])]});
            var Q151;
            Q151=makeQuery(id+"F5.opExtrude","SWEPT_FACE",FACE,{"disambiguationData":[OSD([sQuery(id+"F4.wireOp",EDGE,"E10.sketch_text.stroke-22")])]});
            var Q152;
            Q152=makeQuery(id+"F5.boolean.opBoolean","SPLIT",FACE,{"disambiguationData":[TD([makeQuery(id+"F5.opExtrude","SWEPT_FACE",FACE,{"disambiguationData":[OSD([sQuery(id+"F4.wireOp",EDGE,"E10.sketch_text.stroke-119")])]})])],"derivedFrom":makeQuery(id+"F1.opExtrude","CAP_FACE",FACE,{"disambiguationData":[OSD([sQuery(id+"F0.wireOp",EDGE,"E0.bottom"),sQuery(id+"F0.wireOp",EDGE,"E0.top"),sQuery(id+"F0.wireOp",EDGE,"E0.left"),sQuery(id+"F0.wireOp",EDGE,"E0.right"),sQuery(id+"F0.wireOp",EDGE,"E1"),sQuery(id+"F0.wireOp",EDGE,"E7.MirrorC"),sQuery(id+"F0.wireOp",EDGE,"E8.MirrorC"),sQuery(id+"F0.wireOp",EDGE,"E9.MirrorC")])],"isStart":true})});
            var Q153;
            Q153=makeQuery(id+"F5.boolean.opBoolean","SPLIT",FACE,{"disambiguationData":[TD([makeQuery(id+"F5.opExtrude","SWEPT_FACE",FACE,{"disambiguationData":[OSD([sQuery(id+"F4.wireOp",EDGE,"E10.sketch_text.stroke-158")])]})])],"derivedFrom":makeQuery(id+"F1.opExtrude","CAP_FACE",FACE,{"disambiguationData":[OSD([sQuery(id+"F0.wireOp",EDGE,"E0.bottom"),sQuery(id+"F0.wireOp",EDGE,"E0.top"),sQuery(id+"F0.wireOp",EDGE,"E0.left"),sQuery(id+"F0.wireOp",EDGE,"E0.right"),sQuery(id+"F0.wireOp",EDGE,"E1"),sQuery(id+"F0.wireOp",EDGE,"E7.MirrorC"),sQuery(id+"F0.wireOp",EDGE,"E8.MirrorC"),sQuery(id+"F0.wireOp",EDGE,"E9.MirrorC")])],"isStart":true})});
            var Q154;
            Q154=makeQuery(id+"F5.opExtrude","SWEPT_FACE",FACE,{"disambiguationData":[OSD([sQuery(id+"F4.wireOp",EDGE,"E10.sketch_text.stroke-9")])]});
            var Q155;
            Q155=makeQuery(id+"F5.opExtrude","SWEPT_FACE",FACE,{"disambiguationData":[OSD([sQuery(id+"F4.wireOp",EDGE,"E10.sketch_text.stroke-167")])]});
            var Q156;
            Q156=makeQuery(id+"F5.opExtrude","SWEPT_FACE",FACE,{"disambiguationData":[OSD([sQuery(id+"F4.wireOp",EDGE,"E10.sketch_text.stroke-95")])]});
            var Q157;
            Q157=makeQuery(id+"F5.opExtrude","SWEPT_FACE",FACE,{"disambiguationData":[OSD([sQuery(id+"F4.wireOp",EDGE,"E10.sketch_text.stroke-184")])]});
            var Q158;
            Q158=makeQuery(id+"F5.opExtrude","SWEPT_FACE",FACE,{"disambiguationData":[OSD([sQuery(id+"F4.wireOp",EDGE,"E10.sketch_text.stroke-84")])]});
            var Q159;
            Q159=makeQuery(id+"F5.opExtrude","SWEPT_FACE",FACE,{"disambiguationData":[OSD([sQuery(id+"F4.wireOp",EDGE,"E10.sketch_text.stroke-68")])]});
            var Q160;
            Q160=makeQuery(id+"F5.opExtrude","SWEPT_FACE",FACE,{"disambiguationData":[OSD([sQuery(id+"F4.wireOp",EDGE,"E10.sketch_text.stroke-143")])]});
            var Q161;
            Q161=makeQuery(id+"F5.opExtrude","SWEPT_FACE",FACE,{"disambiguationData":[OSD([sQuery(id+"F4.wireOp",EDGE,"E10.sketch_text.stroke-189")])]});
            var Q162;
            Q162=makeQuery(id+"F5.opExtrude","CAP_FACE",FACE,{"disambiguationData":[OSD([sQuery(id+"F4.wireOp",EDGE,"E10.sketch_text.stroke-13"),sQuery(id+"F4.wireOp",EDGE,"E10.sketch_text.stroke-14"),sQuery(id+"F4.wireOp",EDGE,"E10.sketch_text.stroke-15"),sQuery(id+"F4.wireOp",EDGE,"E10.sketch_text.stroke-16"),sQuery(id+"F4.wireOp",EDGE,"E10.sketch_text.stroke-17"),sQuery(id+"F4.wireOp",EDGE,"E10.sketch_text.stroke-18"),sQuery(id+"F4.wireOp",EDGE,"E10.sketch_text.stroke-19"),sQuery(id+"F4.wireOp",EDGE,"E10.sketch_text.stroke-20")])],"isStart":false});
            var Q163;
            Q163=makeQuery(id+"F5.opExtrude","SWEPT_FACE",FACE,{"disambiguationData":[OSD([sQuery(id+"F4.wireOp",EDGE,"E10.sketch_text.stroke-57")])]});
            var Q164;
            Q164=makeQuery(id+"F5.opExtrude","SWEPT_FACE",FACE,{"disambiguationData":[OSD([sQuery(id+"F4.wireOp",EDGE,"E10.sketch_text.stroke-29")])]});
            var Q165;
            Q165=makeQuery(id+"F5.opExtrude","SWEPT_FACE",FACE,{"disambiguationData":[OSD([sQuery(id+"F4.wireOp",EDGE,"E10.sketch_text.stroke-60")])]});
            var Q166;
            Q166=makeQuery(id+"F5.opExtrude","SWEPT_FACE",FACE,{"disambiguationData":[OSD([sQuery(id+"F4.wireOp",EDGE,"E10.sketch_text.stroke-148")])]});
            var Q167;
            Q167=makeQuery(id+"F5.opExtrude","SWEPT_FACE",FACE,{"disambiguationData":[OSD([sQuery(id+"F4.wireOp",EDGE,"E10.sketch_text.stroke-75")])]});
            var Q168;
            Q168=makeQuery(id+"F5.opExtrude","SWEPT_FACE",FACE,{"disambiguationData":[OSD([sQuery(id+"F4.wireOp",EDGE,"E10.sketch_text.stroke-91")])]});
            var Q169;
            Q169=makeQuery(id+"F5.opExtrude","SWEPT_FACE",FACE,{"disambiguationData":[OSD([sQuery(id+"F4.wireOp",EDGE,"E10.sketch_text.stroke-78")])]});
            var Q170;
            Q170=makeQuery(id+"F5.opExtrude","SWEPT_FACE",FACE,{"disambiguationData":[OSD([sQuery(id+"F4.wireOp",EDGE,"E10.sketch_text.stroke-62")])]});
            var Q171;
            Q171=makeQuery(id+"F5.opExtrude","SWEPT_FACE",FACE,{"disambiguationData":[OSD([sQuery(id+"F4.wireOp",EDGE,"E10.sketch_text.stroke-182")])]});
            var Q172;
            Q172=makeQuery(id+"F5.opExtrude","SWEPT_FACE",FACE,{"disambiguationData":[OSD([sQuery(id+"F4.wireOp",EDGE,"E10.sketch_text.stroke-11")])]});
            var Q173;
            Q173=makeQuery(id+"F5.opExtrude","SWEPT_FACE",FACE,{"disambiguationData":[OSD([sQuery(id+"F4.wireOp",EDGE,"E10.sketch_text.stroke-97")])]});
            var Q174;
            Q174=makeQuery(id+"F5.opExtrude","SWEPT_FACE",FACE,{"disambiguationData":[OSD([sQuery(id+"F4.wireOp",EDGE,"E10.sketch_text.stroke-23")])]});
            var Q175;
            Q175=makeQuery(id+"F5.opExtrude","SWEPT_FACE",FACE,{"disambiguationData":[OSD([sQuery(id+"F4.wireOp",EDGE,"E10.sketch_text.stroke-80")])]});
            var Q176;
            Q176=makeQuery(id+"F5.boolean.opBoolean","SPLIT",FACE,{"disambiguationData":[TD([makeQuery(id+"F5.opExtrude","SWEPT_FACE",FACE,{"disambiguationData":[OSD([sQuery(id+"F4.wireOp",EDGE,"E10.sketch_text.stroke-99")])]})])],"derivedFrom":makeQuery(id+"F1.opExtrude","CAP_FACE",FACE,{"disambiguationData":[OSD([sQuery(id+"F0.wireOp",EDGE,"E0.bottom"),sQuery(id+"F0.wireOp",EDGE,"E0.top"),sQuery(id+"F0.wireOp",EDGE,"E0.left"),sQuery(id+"F0.wireOp",EDGE,"E0.right"),sQuery(id+"F0.wireOp",EDGE,"E1"),sQuery(id+"F0.wireOp",EDGE,"E7.MirrorC"),sQuery(id+"F0.wireOp",EDGE,"E8.MirrorC"),sQuery(id+"F0.wireOp",EDGE,"E9.MirrorC")])],"isStart":true})});
            var Q177;
            Q177=makeQuery(id+"F5.opExtrude","SWEPT_FACE",FACE,{"disambiguationData":[OSD([sQuery(id+"F4.wireOp",EDGE,"E10.sketch_text.stroke-168")])]});
            var Q178;
            Q178=makeQuery(id+"F5.opExtrude","SWEPT_FACE",FACE,{"disambiguationData":[OSD([sQuery(id+"F4.wireOp",EDGE,"E10.sketch_text.stroke-188")])]});
            var Q179;
            Q179=makeQuery(id+"F5.opExtrude","SWEPT_FACE",FACE,{"disambiguationData":[OSD([sQuery(id+"F4.wireOp",EDGE,"E10.sketch_text.stroke-129")])]});
            var Q180;
            Q180=makeQuery(id+"F5.opExtrude","SWEPT_FACE",FACE,{"disambiguationData":[OSD([sQuery(id+"F4.wireOp",EDGE,"E10.sketch_text.stroke-27")])]});
            var Q181;
            Q181=makeQuery(id+"F5.opExtrude","SWEPT_FACE",FACE,{"disambiguationData":[OSD([sQuery(id+"F4.wireOp",EDGE,"E10.sketch_text.stroke-175")])]});
            var Q182;
            Q182=makeQuery(id+"F5.opExtrude","SWEPT_FACE",FACE,{"disambiguationData":[OSD([sQuery(id+"F4.wireOp",EDGE,"E10.sketch_text.stroke-42")])]});
            var Q183;
            Q183=makeQuery(id+"F5.opExtrude","SWEPT_FACE",FACE,{"disambiguationData":[OSD([sQuery(id+"F4.wireOp",EDGE,"E10.sketch_text.stroke-118")])]});
            var Q184;
            Q184=makeQuery(id+"F5.opExtrude","SWEPT_FACE",FACE,{"disambiguationData":[OSD([sQuery(id+"F4.wireOp",EDGE,"E10.sketch_text.stroke-151")])]});
            var Q185;
            Q185=makeQuery(id+"F5.opExtrude","SWEPT_FACE",FACE,{"disambiguationData":[OSD([sQuery(id+"F4.wireOp",EDGE,"E10.sketch_text.stroke-137")])]});
            var Q186;
            Q186=makeQuery(id+"F5.opExtrude","SWEPT_FACE",FACE,{"disambiguationData":[OSD([sQuery(id+"F4.wireOp",EDGE,"E10.sketch_text.stroke-83")])]});
            var Q187;
            Q187=makeQuery(id+"F5.boolean.opBoolean","SPLIT",FACE,{"disambiguationData":[TD([makeQuery(id+"F5.opExtrude","SWEPT_FACE",FACE,{"disambiguationData":[OSD([sQuery(id+"F4.wireOp",EDGE,"E10.sketch_text.stroke-90")])]})])],"derivedFrom":makeQuery(id+"F1.opExtrude","CAP_FACE",FACE,{"disambiguationData":[OSD([sQuery(id+"F0.wireOp",EDGE,"E0.bottom"),sQuery(id+"F0.wireOp",EDGE,"E0.top"),sQuery(id+"F0.wireOp",EDGE,"E0.left"),sQuery(id+"F0.wireOp",EDGE,"E0.right"),sQuery(id+"F0.wireOp",EDGE,"E1"),sQuery(id+"F0.wireOp",EDGE,"E7.MirrorC"),sQuery(id+"F0.wireOp",EDGE,"E8.MirrorC"),sQuery(id+"F0.wireOp",EDGE,"E9.MirrorC")])],"isStart":true})});
            var Q188;
            Q188=makeQuery(id+"F5.opExtrude","SWEPT_FACE",FACE,{"disambiguationData":[OSD([sQuery(id+"F4.wireOp",EDGE,"E10.sketch_text.stroke-139")])]});
            var Q189;
            Q189=makeQuery(id+"F5.opExtrude","SWEPT_FACE",FACE,{"disambiguationData":[OSD([sQuery(id+"F4.wireOp",EDGE,"E10.sketch_text.stroke-70")])]});
            var Q190;
            Q190=makeQuery(id+"F5.opExtrude","SWEPT_FACE",FACE,{"disambiguationData":[OSD([sQuery(id+"F4.wireOp",EDGE,"E10.sketch_text.stroke-160")])]});
            var Q191;
            Q191=makeQuery(id+"F5.opExtrude","SWEPT_FACE",FACE,{"disambiguationData":[OSD([sQuery(id+"F4.wireOp",EDGE,"E10.sketch_text.stroke-71")])]});
            var Q192;
            Q192=makeQuery(id+"F5.opExtrude","SWEPT_FACE",FACE,{"disambiguationData":[OSD([sQuery(id+"F4.wireOp",EDGE,"E10.sketch_text.stroke-117")])]});
            var Q193;
            Q193=makeQuery(id+"F5.opExtrude","SWEPT_FACE",FACE,{"disambiguationData":[OSD([sQuery(id+"F4.wireOp",EDGE,"E10.sketch_text.stroke-147")])]});
            var Q194;
            Q194=makeQuery(id+"F5.opExtrude","SWEPT_FACE",FACE,{"disambiguationData":[OSD([sQuery(id+"F4.wireOp",EDGE,"E10.sketch_text.stroke-164")])]});
            var Q195;
            Q195=makeQuery(id+"F5.opExtrude","SWEPT_FACE",FACE,{"disambiguationData":[OSD([sQuery(id+"F4.wireOp",EDGE,"E10.sketch_text.stroke-61")])]});
            var Q196;
            Q196=makeQuery(id+"F5.opExtrude","SWEPT_FACE",FACE,{"disambiguationData":[OSD([sQuery(id+"F4.wireOp",EDGE,"E10.sketch_text.stroke-19")])]});
            var Q197;
            Q197=makeQuery(id+"F5.opExtrude","SWEPT_FACE",FACE,{"disambiguationData":[OSD([sQuery(id+"F4.wireOp",EDGE,"E10.sketch_text.stroke-35")])]});
            var Q198;
            Q198=makeQuery(id+"F5.opExtrude","SWEPT_FACE",FACE,{"disambiguationData":[OSD([sQuery(id+"F4.wireOp",EDGE,"E10.sketch_text.stroke-140")])]});
            var Q199;
            Q199=makeQuery(id+"F5.opExtrude","SWEPT_FACE",FACE,{"disambiguationData":[OSD([sQuery(id+"F4.wireOp",EDGE,"E10.sketch_text.stroke-20")])]});
            var Q200;
            Q200=makeQuery(id+"F5.opExtrude","SWEPT_FACE",FACE,{"disambiguationData":[OSD([sQuery(id+"F4.wireOp",EDGE,"E10.sketch_text.stroke-16")])]});
            var Q201;
            Q201=makeQuery(id+"F5.opExtrude","SWEPT_FACE",FACE,{"disambiguationData":[OSD([sQuery(id+"F4.wireOp",EDGE,"E10.sketch_text.stroke-18")])]});
            var Q202;
            Q202=makeQuery(id+"F5.opExtrude","SWEPT_FACE",FACE,{"disambiguationData":[OSD([sQuery(id+"F4.wireOp",EDGE,"E10.sketch_text.stroke-17")])]});
            var Q203;
            Q203=qCreatedBy(makeId("Right.planeOp"),FACE);
            mirror(context, id + "F6", {"operationType" : NewBodyOperationType.ADD, "entities" : qUnion([Q0]), "faces" : qUnion([Q1, Q2, Q3, Q4, Q5, Q6, Q7, Q8, Q9, Q10, Q11, Q12, Q13, Q14, Q15, Q16, Q17, Q18, Q19, Q20, Q21, Q22, Q23, Q24, Q25, Q26, Q27, Q28, Q29, Q30, Q31, Q32, Q33, Q34, Q35, Q36, Q37, Q38, Q39, Q40, Q41, Q42, Q43, Q44, Q45, Q46, Q47, Q48, Q49, Q50, Q51, Q52, Q53, Q54, Q55, Q56, Q57, Q58, Q59, Q60, Q61, Q62, Q63, Q64, Q65, Q66, Q67, Q68, Q69, Q70, Q71, Q72, Q73, Q74, Q75, Q76, Q77, Q78, Q79, Q80, Q81, Q82, Q83, Q84, Q85, Q86, Q87, Q88, Q89, Q90, Q91, Q92, Q93, Q94, Q95, Q96, Q97, Q98, Q99, Q100, Q101, Q102, Q103, Q104, Q105, Q106, Q107, Q108, Q109, Q110, Q111, Q112, Q113, Q114, Q115, Q116, Q117, Q118, Q119, Q120, Q121, Q122, Q123, Q124, Q125, Q126, Q127, Q128, Q129, Q130, Q131, Q132, Q133, Q134, Q135, Q136, Q137, Q138, Q139, Q140, Q141, Q142, Q143, Q144, Q145, Q146, Q147, Q148, Q149, Q150, Q151, Q152, Q153, Q154, Q155, Q156, Q157, Q158, Q159, Q160, Q161, Q162, Q163, Q164, Q165, Q166, Q167, Q168, Q169, Q170, Q171, Q172, Q173, Q174, Q175, Q176, Q177, Q178, Q179, Q180, Q181, Q182, Q183, Q184, Q185, Q186, Q187, Q188, Q189, Q190, Q191, Q192, Q193, Q194, Q195, Q196, Q197, Q198, Q199, Q200, Q201, Q202]), "mirrorPlane" : qUnion([Q203])});
        }
    });
